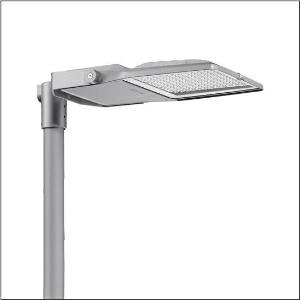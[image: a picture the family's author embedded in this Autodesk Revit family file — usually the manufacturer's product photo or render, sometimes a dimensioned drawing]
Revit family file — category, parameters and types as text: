
# Revit family: floodlight_fl_21_iq_midi___pl33t_5xa7781e2f3a_de32
name_source: partatom
category: Lighting Fixtures
units: mm (PartAtom-declared; Revit-internal decimal feet)

## family parameters
Cut with Voids When Loaded = No
Host = Face
Light Source = No
Part Type = Normal
Room Calculation Point = No
Round Connector Dimension = Use Diameter
Shared = No

## types (1)
- --- (1 x LED, 26540 lm, 208.1 W, 3000K)
    Apparent Load = 208 VA
    CIE Flux Codes = 26 75 99 100 100
    Color Rendering = 70
    Color Temperature = 3000K
    Default Elevation = 1800 mm
    Description = Floodlight FL 21 iQ midi, floodlight, primary light control with lens, of PMMA, primary optical cover: protective disc, of toughened safety glass, transparent, light distribution: PL33T, light emission: direct distribution, installation type: surface-mounted, LED, High Power LED, rated luminous flux: 26.540lm, luminous efficacy: 128lm/W, light colour: 730, colour temperature: 3000K, control gear: ECG iQ, control: optimised constant luminous flux control (CLO 2.0), Desk-Remote (wireless, voltage-free reading and setting of iQ features in the workshop via application-optimized NFC function/RFID function), Light-Fading, Smart-Wire, Night-Set, Lumen-Switch, Temp-Guard, Auto-Match, with terminal, 6-pole, mains connection: 220..240V, AC, 50/60Hz, start of lifetime: 208W, end of service life: 227W, reduction: 90W, luminaire housing, of diecast aluminium, powder-coated, Siteco® metallic grey (DB 702S), corrosivity category C5 mid according to DIN EN ISO 12944, sealing non-destructively replaceable, please order mast flange separately, mast bracket, of steel, galvanised, powder-coated, Siteco® metallic grey (DB 702S), protection rating (complete): IP66, insulation class (complete): insulation class II (safety insulation), certification: CE, ENEC, VDE, protection symbol: D, impact resistance: IK08, permissible operating ambient temperature: -40..+40°C, permissible operating ambient temperature for outdoor applications: -40..+50°C, standard: DIN EN 12944, LABS conformity tested according to VDMA 24364:2018-05, packaging unit: 1 piece

Light Distribution: PL33T
    Height = 76 mm
    Lamp = 1 x LED
    Lamp Light Flux = 26540 lm
    Lamp Power = 208.1 W
    Lamp count = 1
    Length = 657 mm
    Luminous efficacy = 128 lm/W
    Manufacturer = Siteco
    ModVariant = No
    Model = 5XA7781E2F3A
    Number of Poles = 1
    OnlyDefault = Yes
    Power Factor = 1
    Product Name = Floodlight FL 21 iQ midi | PL33T
    Product group = floodlight | pylon annexe
    ProductGroupID = 6200
    Protection Class = Protection class II
    Protection Degree = IP 66
    RLX_Detail_Level = 1
    RLX_Emergency_Light_Flux = 0 lm
    RLX_Emergency_Type = 0
    RLX_Emergency_Type_DB = No
    RlxData = <blob elided: 153645 chars, md5=ec447ea3>
    Socket = socket
    Standby Power = 0 W
    System Light Flux = 26540 lm
    System Power = 208 W
    Type Comments = factory setting: luminous flux: 100 % | dim-lin: 254 | 710 mA
    Type Image = l_1007123.jpg
    URL = http://relux.com
    VarID = @adj_072867
    Voltage = 0 V
    Weight = 0.00 kg
    Width = 442 mm

## geometry (parser evidence)
native form markers: Blend x4, Sweep x13
no freeform markers — native parametric forms only
